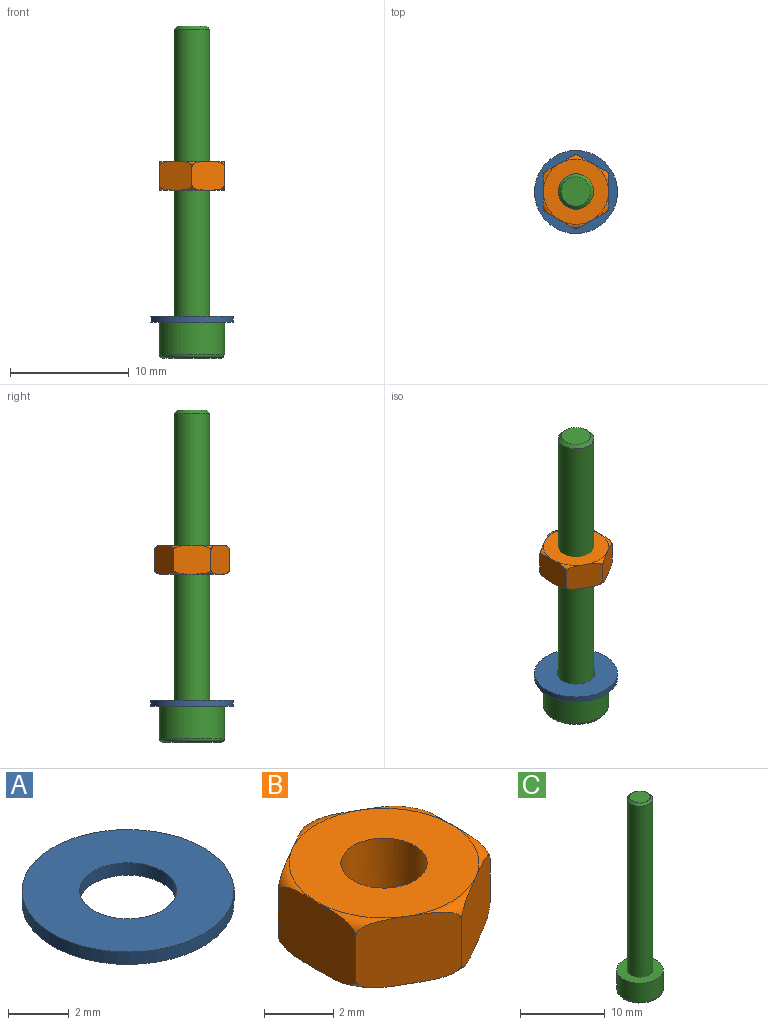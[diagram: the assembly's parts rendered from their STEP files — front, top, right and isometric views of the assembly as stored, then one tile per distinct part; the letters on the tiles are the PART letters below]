
ASSEMBLY  parts=3 mates=3
PART A: 4 faces, bbox 7x7x0.5 mm
  f0: cylinder r=1.6mm len=3.2mm, axis (0,0,-1), area 5mm2, adj f2,f3
  f1: cylinder r=3.5mm len=7mm, axis (0,0,-1), area 11mm2, adj f2,f3
  f2: plane 7x7mm, normal (0,0,1), area 30.4mm2, adj f0,f1
  f3: plane 7x7mm, normal (0,0,-1), area 30.4mm2, adj f0,f1
PART B: 11 faces, bbox 6.9x6.9x2.4 mm
  f0: plane 5.49x5.49mm, normal (0,0,1), area 18.8mm2, adj f1,f10
  f1: torus R=2.75mm, axis (0,0,-1), area 2.8mm2, adj f0,f2,f3,f4,f5,f6,f7
  f2: plane 2.75x2.4mm, normal (0.5,0.87,0), area 7.3mm2, adj f1,f3,f7,f9
  f3: plane 3.18x2.4mm, normal (1,0,0), area 7.3mm2, adj f1,f2,f4,f9
  f4: plane 2.75x2.4mm, normal (0.5,-0.87,0), area 7.3mm2, adj f1,f3,f5,f9
  f5: plane 2.75x2.4mm, normal (-0.5,-0.87,0), area 7.3mm2, adj f1,f4,f6,f9
  f6: plane 3.18x2.4mm, normal (-1,0,0), area 7.3mm2, adj f1,f5,f7,f9
  f7: plane 2.75x2.4mm, normal (-0.5,0.87,0), area 7.3mm2, adj f1,f2,f6,f9
  f8: plane 5.49x5.49mm, normal (0,0,-1), area 18.8mm2, adj f9,f10
  f9: torus R=2.75mm, axis (0,0,-1), area 2.8mm2, adj f2,f3,f4,f5,f6,f7,f8
  f10: cylinder r=1.25mm len=2.5mm, axis (0,0,-1), area 18.8mm2, adj f0,f8
PART C: 14 faces, bbox 6x6x28 mm
  f0: plane 4.95x4.95mm, normal (0,0,-1), area 13.5mm2, adj f3,f4,f5,f6,f7,f8,f9
  f1: cylinder r=2.75mm len=5.5mm, axis (0,0,1), area 47.1mm2, adj f2,f3
  f2: plane 5.5x5.5mm, normal (0,0,1), area 16.7mm2, adj f1,f11
  f3: torus R=2.48mm, axis (0,0,-1), area 7.2mm2, adj f0,f1
  f4: plane 1.5x1.49mm, normal (-1,0,0), area 2.2mm2, adj f0,f5,f9,f10
  f5: plane 1.5x1.29mm, normal (-0.5,-0.87,0), area 2.2mm2, adj f0,f4,f6,f10
  f6: plane 1.5x1.29mm, normal (0.5,-0.87,0), area 2.2mm2, adj f0,f5,f7,f10
  f7: plane 1.5x1.49mm, normal (1,0,0), area 2.2mm2, adj f0,f6,f8,f10
  f8: plane 1.5x1.29mm, normal (0.5,0.87,0), area 2.2mm2, adj f0,f7,f9,f10
  f9: plane 1.5x1.29mm, normal (-0.5,0.87,0), area 2.2mm2, adj f0,f4,f8,f10
  f10: plane 2.98x2.58mm, normal (0,0,-1), area 5.8mm2, adj f4,f5,f6,f7,f8,f9
  f11: cylinder r=1.5mm len=24.73mm, axis (0,0,-1), area 233.1mm2, adj f2,f13
  f12: plane 2.46x2.46mm, normal (0,0,1), area 4.7mm2, adj f13
  f13: cone r=1.23mm half-angle=45deg, axis (0,0,-1), area 3.3mm2, adj f11,f12
PLACE A t=(70.58,80.11,41.04)mm
PLACE B t=(40.58,90.11,52.2)mm
PLACE C t=(-9.42,70.11,41.04)mm
MATE planar C.f1 <-> A.f0  axis (0,0,1) through (60.58,70.11,41.04)mm
MATE cylindrical C.f1 <-> B.f1  axis (0,0,-1) through (60.58,70.11,53.4)mm
MATE cylindrical A.f0 <-> C.f1  axis (0,0,-1) through (60.58,70.11,41.04)mm
